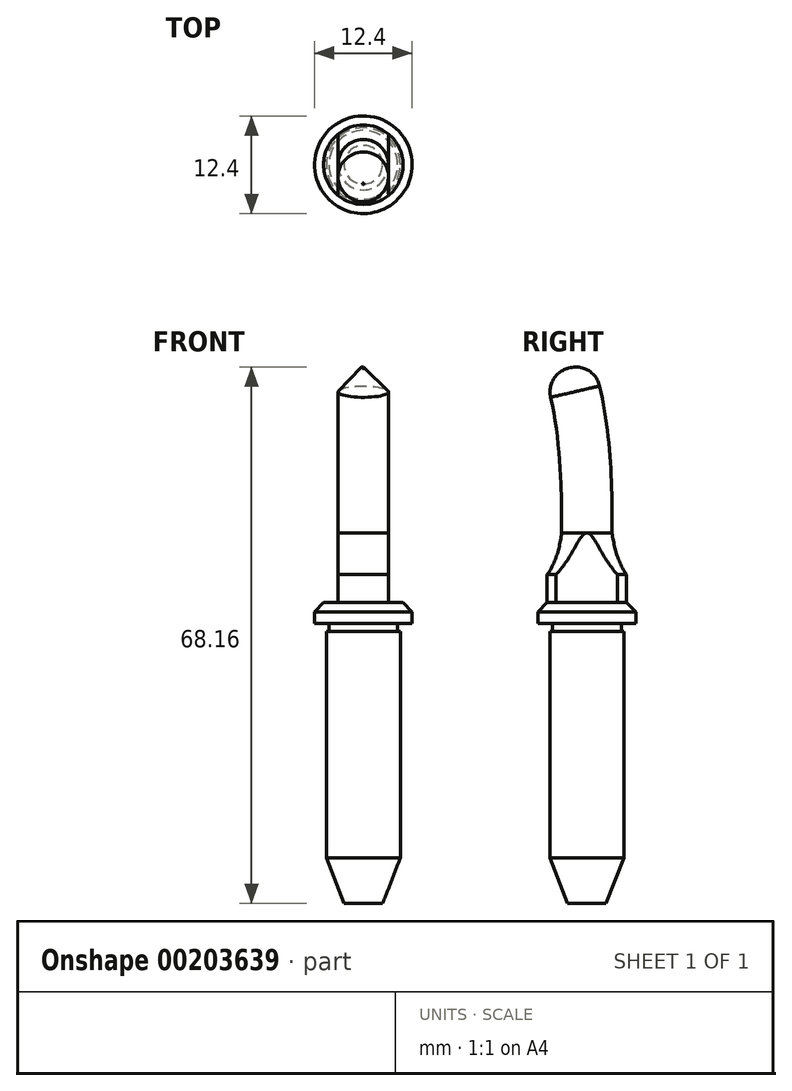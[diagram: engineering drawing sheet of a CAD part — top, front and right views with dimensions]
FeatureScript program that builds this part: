
annotation { "Feature Type Name" : "Feature", "Feature Type Description" : "" }
export const myFeature = defineFeature(function(context is Context, id is Id, definition is map)
    precondition{}
    {
        {
            var Q0;
            Q0=qCreatedBy(makeId("Front.planeOp"),FACE);
            var sketch = newSketch(context, id + "F0", { "sketchPlane" : qUnion([Q0])});
            skLineSegment(sketch, "E0", {"start": v(0, 0) * mm, "end": v(2.45, 0) * mm});
            skLineSegment(sketch, "E1", {"start": v(2.45, 0) * mm, "end": v(4.7, 5.78) * mm});
            skLineSegment(sketch, "E2", {"start": v(4.7, 5.78) * mm, "end": v(4.7, 34.58) * mm});
            skLineSegment(sketch, "E3", {"start": v(4.7, 34.58) * mm, "end": v(4.37, 34.58) * mm});
            skLineSegment(sketch, "E4", {"start": v(4.37, 34.58) * mm, "end": v(4.37, 35.58) * mm});
            skLineSegment(sketch, "E5", {"start": v(4.37, 35.58) * mm, "end": v(6.2, 35.58) * mm});
            skLineSegment(sketch, "E6", {"start": v(6.2, 35.58) * mm, "end": v(6.2, 37.08) * mm});
            skLineSegment(sketch, "E7", {"start": v(6.2, 37.08) * mm, "end": v(0, 37.08) * mm});
            skLineSegment(sketch, "E8", {"start": v(0, 37.08) * mm, "end": v(0, 0) * mm});
            skLineSegment(sketch, "E9", {"start": v(5.05, 37.08) * mm, "end": v(5.05, 41.78) * mm});
            skLineSegment(sketch, "E10", {"start": v(0, 37.08) * mm, "end": v(0, 47.08) * mm});
            skLineSegment(sketch, "E11", {"start": v(0, 47.08) * mm, "end": v(3.2, 47.08) * mm});
            skFitSpline(sketch, "E12", {"points": [v(3.2, 47.08) * mm, v(5.05, 41.78) * mm], "startDerivative": vector(0.9, -6.3) * mm, "endDerivative": vector(3.14, -4.43) * mm});
            skLineSegment(sketch, "E13", {"start": v(6.2, 37.08) * mm, "end": v(5.05, 38.23) * mm});
            skSolve(sketch);
        }
        {
            var Q0;
            {var subQ0=sQuery(id+"F0.wireOp",EDGE,"E10");Q0=makeQuery(id+"F0.imprint","IMPRINT",FACE,{"disambiguationData":[TD([[makeQuery(id+"F0.imprint","IMPRINT",EDGE,{"derivedFrom":subQ0}),-1.0]])]});}
            var Q1;
            {var subQ0=sQuery(id+"F0.wireOp",EDGE,"E13");Q1=makeQuery(id+"F0.imprint","IMPRINT",FACE,{"disambiguationData":[TD([[makeQuery(id+"F0.imprint","IMPRINT",EDGE,{"derivedFrom":subQ0}),1.0]])]});}
            var Q2;
            Q2=makeQuery(id+"F0.imprint","IMPRINT",FACE,{"disambiguationData":[TD([[makeQuery(id+"F0.imprint","IMPRINT",EDGE,{"derivedFrom":sQuery(id+"F0.wireOp",EDGE,"E0")}),1.0]])]});
            var Q3;
            Q3=sQuery(id+"F0.wireOp",EDGE,"E8");
            revolve(context, id + "F1", {"entities" : qUnion([Q0, Q1, Q2]), "axis" : qUnion([Q3]), "revolveType" : RevolveType.FULL});
        }
        {
            var Q0;
            Q0=qCreatedBy(makeId("Front.planeOp"),FACE);
            var sketch = newSketch(context, id + "F2", { "sketchPlane" : qUnion([Q0])});
            skLineSegment(sketch, "E14.0", {"start": v(-3.2, 47.08) * mm, "end": v(3.2, 47.08) * mm});
            skLineSegment(sketch, "E15.bottom", {"start": v(3.2, 47.08) * mm, "end": v(5.34, 47.08) * mm});
            skLineSegment(sketch, "E15.top", {"start": v(3.2, 38.23) * mm, "end": v(5.34, 38.23) * mm});
            skLineSegment(sketch, "E15.left", {"start": v(3.2, 47.08) * mm, "end": v(3.2, 38.23) * mm});
            skLineSegment(sketch, "E15.right", {"start": v(5.34, 47.08) * mm, "end": v(5.34, 38.23) * mm});
            skLineSegment(sketch, "E16.bottom", {"start": v(-3.2, 47.08) * mm, "end": v(-5.6, 47.08) * mm});
            skLineSegment(sketch, "E16.top", {"start": v(-3.2, 38.23) * mm, "end": v(-5.6, 38.23) * mm});
            skLineSegment(sketch, "E16.left", {"start": v(-3.2, 47.08) * mm, "end": v(-3.2, 38.23) * mm});
            skLineSegment(sketch, "E16.right", {"start": v(-5.6, 47.08) * mm, "end": v(-5.6, 38.23) * mm});
            skLineSegment(sketch, "E17.0", {"start": v(-5.05, 38.23) * mm, "end": v(5.05, 38.23) * mm});
            skSolve(sketch);
        }
        {
            var Q0;
            Q0=makeQuery(id+"F2.imprint","IMPRINT",FACE,{"disambiguationData":[TD([[makeQuery(id+"F2.imprint","IMPRINT",EDGE,{"derivedFrom":sQuery(id+"F2.wireOp",EDGE,"E16.bottom")}),1.0]])]});
            var Q1;
            Q1=makeQuery(id+"F2.imprint","IMPRINT",FACE,{"disambiguationData":[TD([[makeQuery(id+"F2.imprint","IMPRINT",EDGE,{"derivedFrom":sQuery(id+"F2.wireOp",EDGE,"E15.bottom")}),-1.0]])]});
            extrude(context, id + "F3", {"entities" : qUnion([Q0, Q1]), "operationType" : NewBodyOperationType.REMOVE, "oppositeDirection" : true, "depth" : 5 * mm, "hasSecondDirection" : true, "secondDirectionOppositeDirection" : false, "secondDirectionDepth" : 5 * mm});
        }
        {
            var Q0;
            Q0=qCreatedBy(makeId("Right.planeOp"),FACE);
            var sketch = newSketch(context, id + "F4", { "sketchPlane" : qUnion([Q0])});
            skFitSpline(sketch, "E18", {"points": [v(0, 47.08) * mm, v(-2.3, 68.03) * mm], "startDerivative": vector(0, 16.13) * mm, "endDerivative": vector(-6.9, 22.3) * mm});
            skSolve(sketch);
        }
        {
            var Q0;
            Q0=makeQuery(id+"F1.opRevolve","SWEPT_FACE",FACE,{"disambiguationData":[OSD([sQuery(id+"F0.wireOp",EDGE,"E11")])]});
            var Q1;
            Q1=sQuery(id+"F4.wireOp",EDGE,"E18");
            sweep(context, id + "F5", {"operationType" : NewBodyOperationType.ADD, "profiles" : qUnion([Q0]), "path" : qUnion([Q1])});
        }
        {
            var Q0;
            Q0=makeQuery(id+"F5.opSweep","CAP_EDGE",EDGE,{"disambiguationData":[OSD([sQuery(id+"F0.wireOp",EDGE,"E11"),sQuery(id+"F0.wireOp",EDGE,"E12"),sQuery(id+"F4.wireOp",VERTEX,"E18.end")])],"isStart":false});
            fillet(context, id + "F6", {"entities" : qUnion([Q0]), "radius" : 3.1 * mm, "tangentPropagation" : true, "allowEdgeOverflow" : false});
        }
    });
